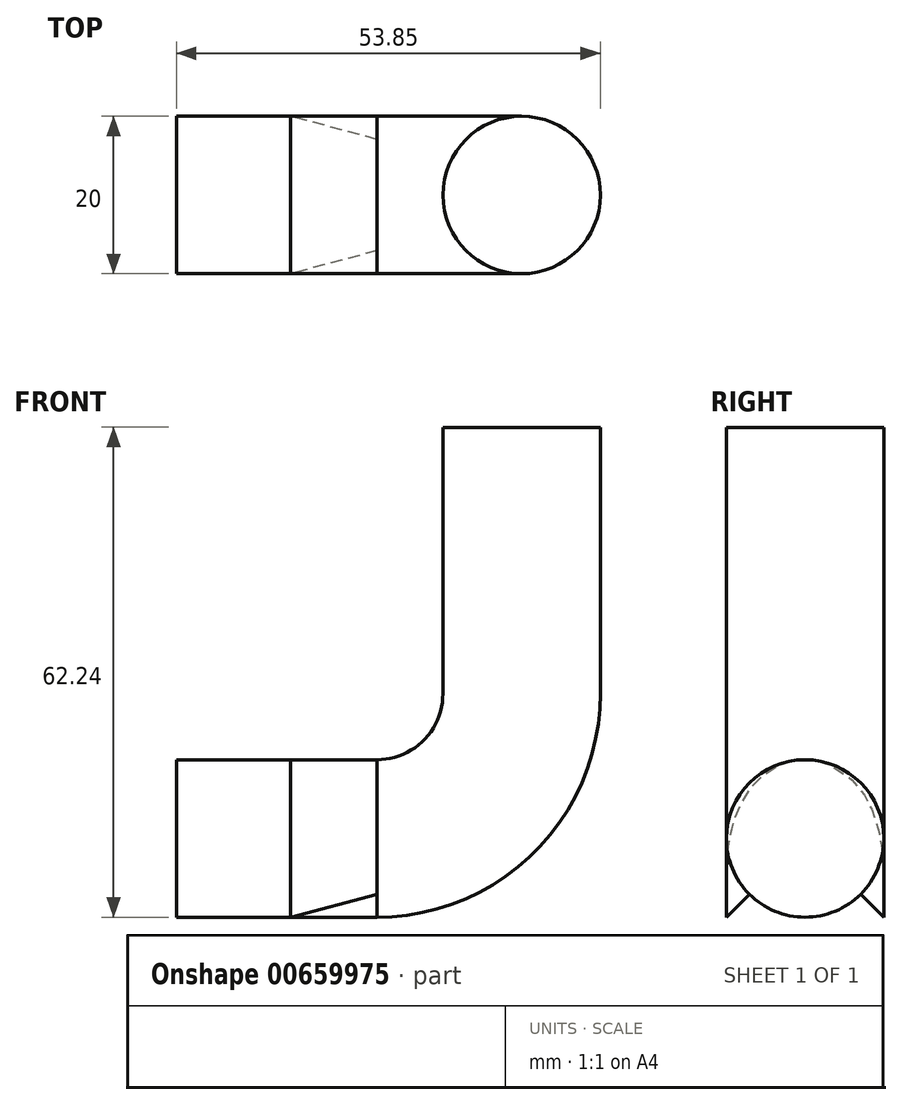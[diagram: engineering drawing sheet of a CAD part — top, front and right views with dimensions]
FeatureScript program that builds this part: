
annotation { "Feature Type Name" : "Feature", "Feature Type Description" : "" }
export const myFeature = defineFeature(function(context is Context, id is Id, definition is map)
    precondition{}
    {
        {
            var Q0;
            Q0=qCreatedBy(makeId("Front.planeOp"),FACE);
            var sketch = newSketch(context, id + "F0", { "sketchPlane" : qUnion([Q0])});
            skLineSegment(sketch, "E0", {"start": v(43.85, -8.95) * mm, "end": v(43.85, 24.9) * mm});
            skArc(sketch, "E1", {"start": v(43.85, -8.95) * mm, "mid": v(38.46, -21.95) * mm, "end": v(25.45, -27.34) * mm});
            skLineSegment(sketch, "E2", {"start": v(0, -27.34) * mm, "end": v(14.5, -27.34) * mm});
            skLineSegment(sketch, "E3", {"start": v(14.5, -27.34) * mm, "end": v(25.45, -27.34) * mm});
            skSolve(sketch);
        }
        {
            var Q0;
            Q0=qCreatedBy(makeId("Right.planeOp"),FACE);
            var sketch = newSketch(context, id + "F1", { "sketchPlane" : qUnion([Q0])});
            skLineSegment(sketch, "E4.bottom", {"start": v(10, -37.34) * mm, "end": v(-10, -37.34) * mm});
            skLineSegment(sketch, "E4.top", {"start": v(10, -27.34) * mm, "end": v(-10, -27.34) * mm, "construction": true});
            skLineSegment(sketch, "E4.left", {"start": v(10, -37.34) * mm, "end": v(10, -27.34) * mm});
            skLineSegment(sketch, "E4.right", {"start": v(-10, -37.34) * mm, "end": v(-10, -27.34) * mm});
            skPoint(sketch, "E4.middle", {"position": v(0, -32.34) * mm});
            skArc(sketch, "E5", {"start": v(10, -27.34) * mm, "mid": v(0, -17.34) * mm, "end": v(-10, -27.34) * mm});
            skLineSegment(sketch, "E6", {"start": v(0, -17.34) * mm, "end": v(0, -37.34) * mm, "construction": true});
            skSolve(sketch);
        }
        {
            var Q0;
            Q0=makeQuery(id+"F1.imprint","IMPRINT",FACE,{"disambiguationData":[TD([[makeQuery(id+"F1.imprint","IMPRINT",EDGE,{"derivedFrom":sQuery(id+"F1.wireOp",EDGE,"E4.bottom")}),-1.0]])]});
            var Q1;
            Q1=sQuery(id+"F0.wireOp",EDGE,"E2");
            sweep(context, id + "F2", {"profiles" : qUnion([Q0]), "path" : qUnion([Q1])});
        }
        {
            var Q0;
            Q0=sQuery(id+"F0.wireOp",VERTEX,"E0.end");
            var Q1;
            Q1=sQuery(id+"F0.wireOp",EDGE,"E0");
            cPlane(context, id + "F3", {"entities" : qUnion([Q0, Q1]), "cplaneType" : CPlaneType.CURVE_POINT, "offset" : 25 * mm, "width" : 150 * mm, "height" : 150 * mm});
        }
        {
            var Q0;
            Q0=qCreatedBy(id+"F3.planeOp",FACE);
            var sketch = newSketch(context, id + "F4", { "sketchPlane" : qUnion([Q0])});
            skCircle(sketch, "E7", {"center": v(43.85, 0) * mm, "radius": 10 * mm});
            skSolve(sketch);
        }
        {
            var Q0;
            Q0=makeQuery(id+"F4.imprint","IMPRINT",FACE,{"disambiguationData":[TD([[makeQuery(id+"F4.imprint","IMPRINT",EDGE,{"derivedFrom":sQuery(id+"F4.wireOp",EDGE,"E7")}),1.0]])]});
            var Q1;
            Q1=sQuery(id+"F0.wireOp",EDGE,"E0");
            var Q2;
            Q2=sQuery(id+"F0.wireOp",EDGE,"E1");
            sweep(context, id + "F5", {"profiles" : qUnion([Q0]), "path" : qUnion([Q1, Q2])});
        }
        {
            var Q1;
            Q1=makeQuery(id+"F5.opSweep","CAP_FACE",FACE,{"disambiguationData":[OSD([sQuery(id+"F0.wireOp",VERTEX,"E1.end"),sQuery(id+"F4.wireOp",EDGE,"E7")])],"isStart":false});
            var Q2;
            Q2=makeQuery(id+"F2.opSweep","CAP_FACE",FACE,{"disambiguationData":[OSD([sQuery(id+"F0.wireOp",VERTEX,"E2.end"),sQuery(id+"F1.wireOp",EDGE,"E4.bottom"),sQuery(id+"F1.wireOp",EDGE,"E4.left"),sQuery(id+"F1.wireOp",EDGE,"E4.right"),sQuery(id+"F1.wireOp",EDGE,"E5")])],"isStart":false});
            loft(context, id + "F6", {"operationType" : NewBodyOperationType.ADD, "sheetProfilesArray" : [{ "sheetProfileEntities" : qUnion([Q1]) }, { "sheetProfileEntities" : qUnion([Q2]) }]});
        }
    });
